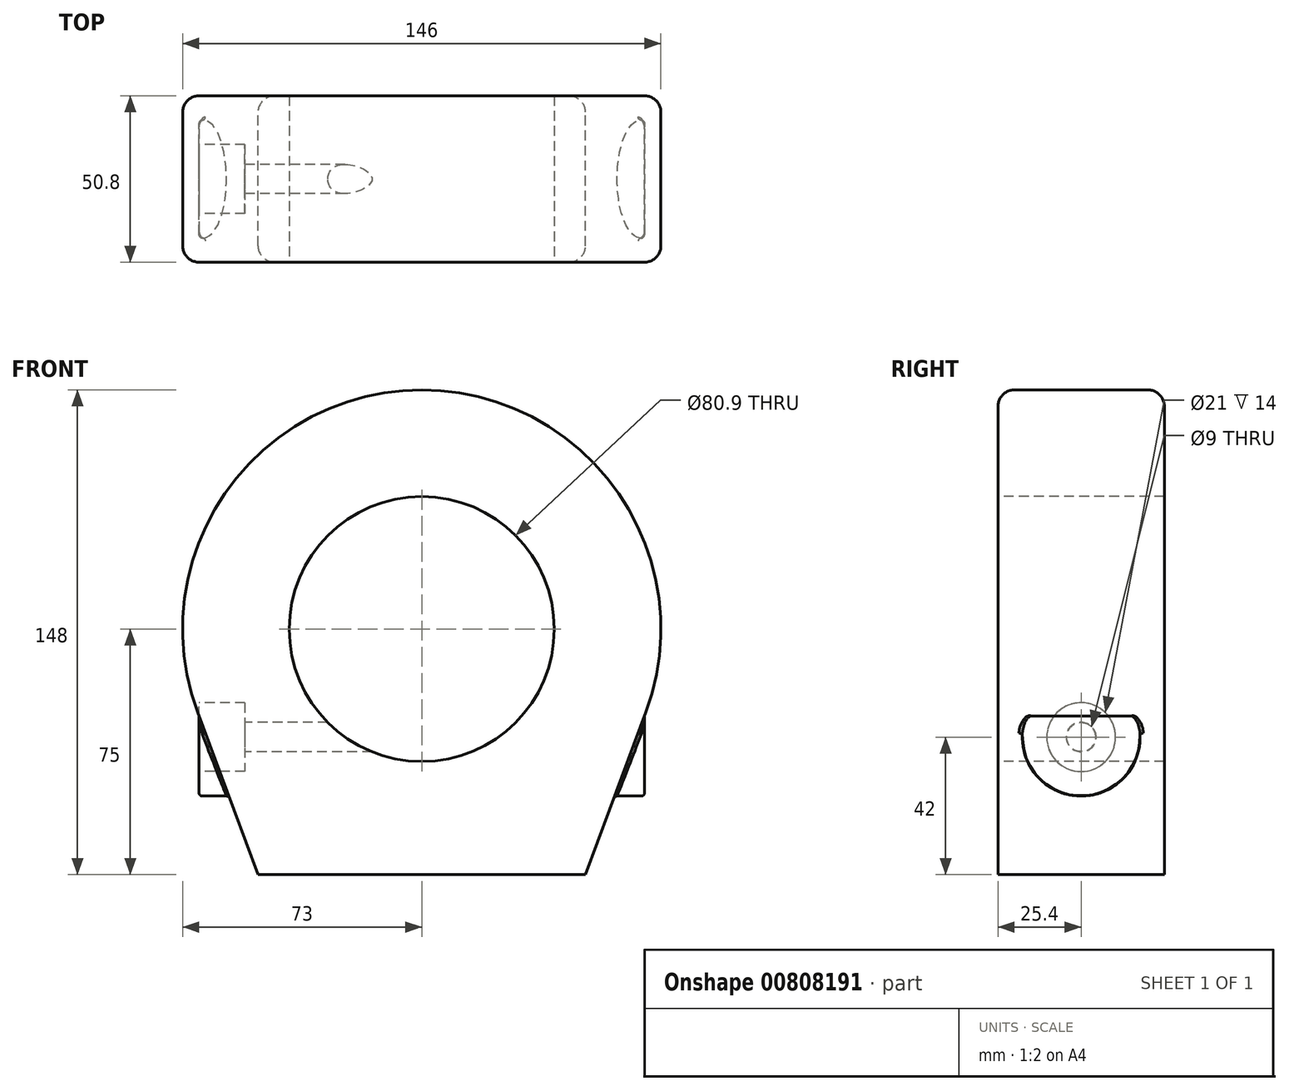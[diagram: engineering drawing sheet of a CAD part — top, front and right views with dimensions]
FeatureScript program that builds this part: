
annotation { "Feature Type Name" : "Feature", "Feature Type Description" : "" }
export const myFeature = defineFeature(function(context is Context, id is Id, definition is map)
    precondition{}
    {
        {
            var Q0;
            Q0=qCreatedBy(makeId("Front.planeOp"),FACE);
            var sketch = newSketch(context, id + "F0", { "sketchPlane" : qUnion([Q0])});
            skCircle(sketch, "E0", {"center": v(0, 0) * mm, "radius": 73 * mm});
            skLineSegment(sketch, "E1", {"start": v(-50, -75) * mm, "end": v(50, -75) * mm});
            skLineSegment(sketch, "E2", {"start": v(0, 0) * mm, "end": v(0, -75) * mm, "construction": true});
            skLineSegment(sketch, "E3", {"start": v(-50, -75) * mm, "end": v(-68.42, -25.44) * mm});
            skLineSegment(sketch, "E4", {"start": v(50, -75) * mm, "end": v(68.42, -25.44) * mm});
            skSolve(sketch);
        }
        {
            var Q0;
            Q0 = qSketchRegion(id + "F0", true);
            extrude(context, id + "F1", {"entities" : qUnion([Q0]), "depth" : 50.8 * mm, "offsetDistance" : 25 * mm});
        }
        {
            var Q0;
            Q0=makeQuery(id+"F1.opExtrude","CAP_EDGE",EDGE,{"disambiguationData":[OSD([sQuery(id+"F0.wireOp",EDGE,"E4")])],"isStart":false});
            var Q1;
            Q1=makeQuery(id+"F1.opExtrude","CAP_EDGE",EDGE,{"disambiguationData":[OSD([sQuery(id+"F0.wireOp",EDGE,"E4")])],"isStart":true});
            fillet(context, id + "F2", {"entities" : qUnion([Q0, Q1]), "radius" : 5 * mm, "tangentPropagation" : true, "allowEdgeOverflow" : false});
        }
        {
            var Q0;
            Q0=makeQuery(id+"F1.opExtrude","CAP_FACE",FACE,{"disambiguationData":[OSD([sQuery(id+"F0.wireOp",EDGE,"E0"),sQuery(id+"F0.wireOp",EDGE,"E1"),sQuery(id+"F0.wireOp",EDGE,"E3"),sQuery(id+"F0.wireOp",EDGE,"E4")])],"isStart":false});
            var sketch = newSketch(context, id + "F3", { "sketchPlane" : qUnion([Q0])});
            skCircle(sketch, "E5", {"center": v(0, 0) * mm, "radius": 40.45 * mm});
            skSolve(sketch);
        }
        {
            var Q0;
            Q0 = qSketchRegion(id + "F3", true);
            extrude(context, id + "F4", {"entities" : qUnion([Q0]), "operationType" : NewBodyOperationType.REMOVE, "endBound" : BoundingType.THROUGH_ALL, "oppositeDirection" : true, "depth" : 25 * mm, "offsetDistance" : 25 * mm});
        }
        {
            var Q0;
            Q0=qCreatedBy(makeId("Right.planeOp"),FACE);
            cPlane(context, id + "F5", {"entities" : qUnion([Q0]), "cplaneType" : CPlaneType.OFFSET, "offset" : 68 * mm, "oppositeDirection" : true, "width" : 150 * mm, "height" : 150 * mm});
        }
        {
            var Q0;
            Q0=qCreatedBy(id+"F5.planeOp",FACE);
            var sketch = newSketch(context, id + "F6", { "sketchPlane" : qUnion([Q0])});
            skCircle(sketch, "E6", {"center": v(-25.4, -33) * mm, "radius": 18 * mm});
            skSolve(sketch);
        }
        {
            var Q0;
            Q0 = qSketchRegion(id + "F6", true);
            extrude(context, id + "F7", {"entities" : qUnion([Q0]), "operationType" : NewBodyOperationType.ADD, "depth" : 12 * mm, "offsetDistance" : 25 * mm});
        }
        {
            var Q0;
            Q0=makeQuery(id+"F7.opExtrude","CAP_EDGE",EDGE,{"disambiguationData":[OSD([sQuery(id+"F6.wireOp",EDGE,"E6")])],"isStart":true});
            var Q1;
            Q1=makeQuery(id+"F7.boolean.opBoolean","INTERSECT",EDGE,{"derivedFrom":[makeQuery(id+"F1.opExtrude","SWEPT_FACE",FACE,{"disambiguationData":[OSD([sQuery(id+"F0.wireOp",EDGE,"E3")])]}),makeQuery(id+"F7.opExtrude","SWEPT_FACE",FACE,{"disambiguationData":[OSD([sQuery(id+"F6.wireOp",EDGE,"E6")])]})]});
            fillet(context, id + "F8", {"entities" : qUnion([Q0, Q1]), "radius" : 1 * mm, "tangentPropagation" : true, "allowEdgeOverflow" : false});
        }
        {
            var Q0;
            Q0=makeQuery(id+"F1.opExtrude","SWEPT_BODY",BODY,{"disambiguationData":[OSD([sQuery(id+"F0.wireOp",EDGE,"E0"),sQuery(id+"F0.wireOp",EDGE,"E1"),sQuery(id+"F0.wireOp",EDGE,"E3"),sQuery(id+"F0.wireOp",EDGE,"E4")])]});
            var Q1;
            Q1=qCreatedBy(makeId("Right.planeOp"),FACE);
            mirror(context, id + "F9", {"operationType" : NewBodyOperationType.ADD, "entities" : qUnion([Q0]), "mirrorPlane" : qUnion([Q1])});
        }
        {
            var Q0;
            Q0=makeQuery(id+"F7.opExtrude","CAP_FACE",FACE,{"disambiguationData":[OSD([sQuery(id+"F6.wireOp",EDGE,"E6")])],"isStart":true});
            var sketch = newSketch(context, id + "F10", { "sketchPlane" : qUnion([Q0])});
            skCircle(sketch, "E7", {"center": v(25.4, -33) * mm, "radius": 10.5 * mm});
            skSolve(sketch);
        }
        {
            var Q0;
            Q0 = qSketchRegion(id + "F10", true);
            extrude(context, id + "F11", {"entities" : qUnion([Q0]), "operationType" : NewBodyOperationType.REMOVE, "oppositeDirection" : true, "depth" : 14 * mm, "offsetDistance" : 25 * mm});
        }
        {
            var Q0;
            Q0=makeQuery(id+"F11.boolean.opBoolean","COPY",FACE,{"derivedFrom":makeQuery(id+"F11.opExtrude","CAP_FACE",FACE,{"disambiguationData":[OSD([sQuery(id+"F10.wireOp",EDGE,"E7")])],"isStart":false})});
            var sketch = newSketch(context, id + "F12", { "sketchPlane" : qUnion([Q0])});
            skCircle(sketch, "E8", {"center": v(25.4, -33) * mm, "radius": 4.5 * mm});
            skSolve(sketch);
        }
        {
            var Q0;
            Q0 = qSketchRegion(id + "F12", true);
            extrude(context, id + "F13", {"entities" : qUnion([Q0]), "operationType" : NewBodyOperationType.REMOVE, "oppositeDirection" : true, "depth" : 50.5 * mm, "offsetDistance" : 25 * mm});
        }
    });
